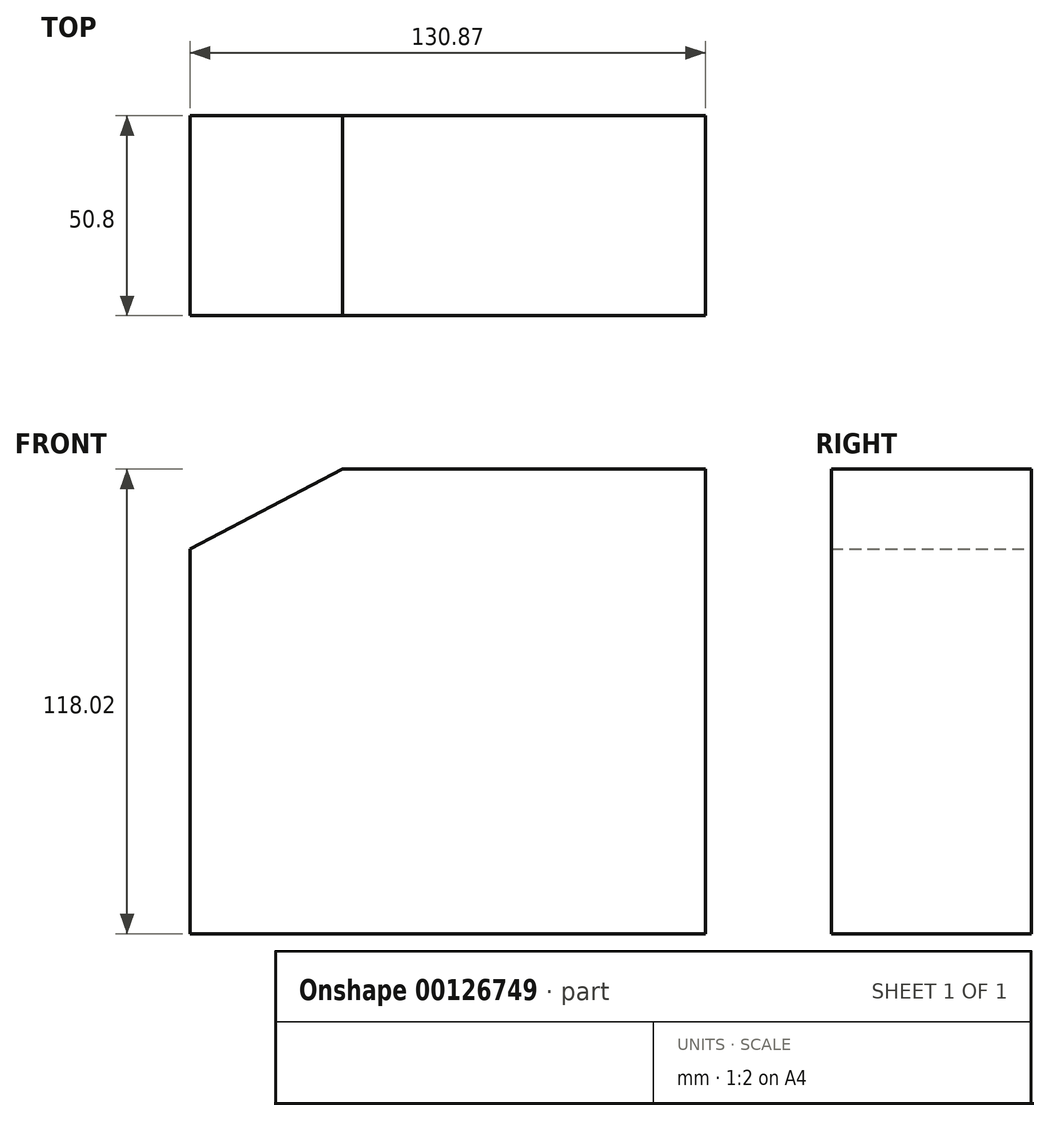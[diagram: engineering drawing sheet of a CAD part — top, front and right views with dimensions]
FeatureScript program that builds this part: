
annotation { "Feature Type Name" : "Feature", "Feature Type Description" : "" }
export const myFeature = defineFeature(function(context is Context, id is Id, definition is map)
    precondition{}
    {
        {
            var Q0;
            Q0=qCreatedBy(makeId("Front.planeOp"),FACE);
            var sketch = newSketch(context, id + "F0", { "sketchPlane" : qUnion([Q0])});
            skLineSegment(sketch, "E0.top", {"start": v(-60.53, -52.25) * mm, "end": v(70.34, -52.25) * mm});
            skLineSegment(sketch, "E0.left", {"start": v(-60.53, 45.48) * mm, "end": v(-60.53, -52.25) * mm});
            skLineSegment(sketch, "E0.right", {"start": v(70.34, 65.77) * mm, "end": v(70.34, -52.25) * mm});
            skLineSegment(sketch, "E1", {"start": v(-60.53, 45.48) * mm, "end": v(-21.81, 65.77) * mm});
            skLineSegment(sketch, "E2", {"start": v(-21.81, 65.77) * mm, "end": v(70.34, 65.77) * mm});
            skSolve(sketch);
        }
        {
            var Q0;
            Q0=makeQuery(id+"F0.imprint","IMPRINT",FACE,{"disambiguationData":[TD([[makeQuery(id+"F0.imprint","IMPRINT",EDGE,{"derivedFrom":sQuery(id+"F0.wireOp",EDGE,"E0.top")}),1.0]])]});
            extrude(context, id + "F1", {"entities" : qUnion([Q0]), "depth" : 25.4 * mm, "hasSecondDirection" : true, "secondDirectionOppositeDirection" : true, "secondDirectionDepth" : 25.4 * mm});
        }
    });
